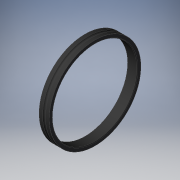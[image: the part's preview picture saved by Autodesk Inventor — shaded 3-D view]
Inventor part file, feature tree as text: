
AUTODESK INVENTOR PART (.ipt)
format: ipt  version: 2019 (Build 230136000, 136)  size: 175,616 bytes
history: native  units: mm
features: other x7, revolve x1, sketch x1
ambient origin geometry x8: Origin, YZ Plane, XZ Plane, XY Plane, X Axis, Y Axis, Z Axis, Center Point
bodies: Solid1 (feature_tree)
feature tree (9):
  revolve  "Revolution1"  [1 undecoded]
  other  "ir_XY"
  other  "ir_YZ"
  other  "ir_ZX"
  other  "ir_X"
  other  "ir_Y"
  other  "ir_Z"
  other  "ir_Center"
  sketch  "Sketch_10"  dims[d0=360.0deg]
note: 1 required parameter value undecoded (feature->parameter linkage not recoverable at this tier; creation-order binding heuristic only, values carry confidence <= 0.55)
